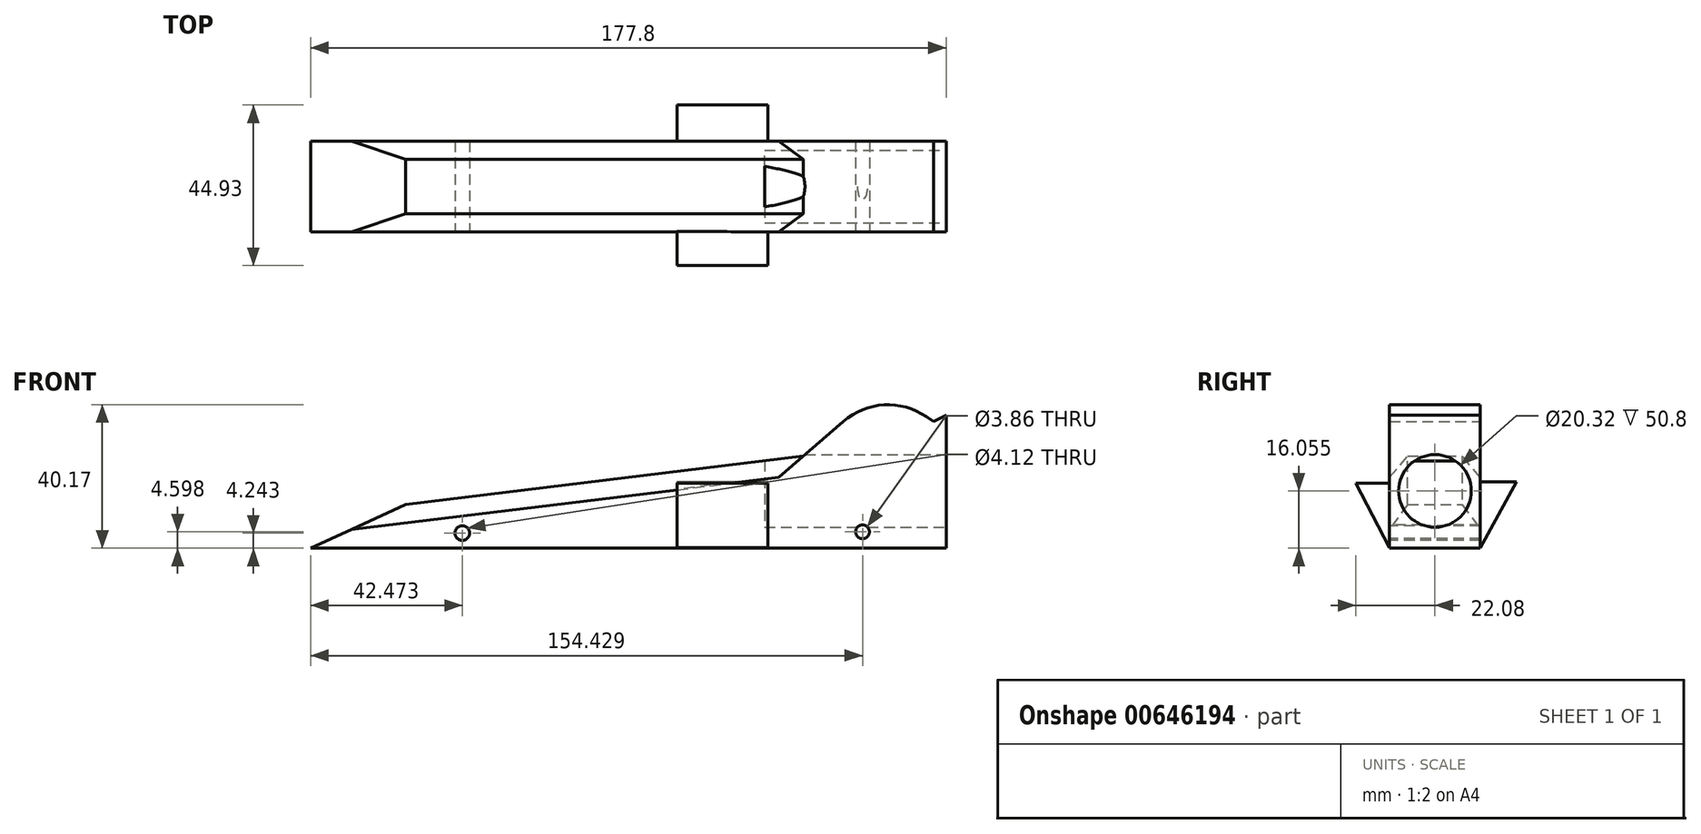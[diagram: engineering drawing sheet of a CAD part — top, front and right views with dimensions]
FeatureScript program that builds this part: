
annotation { "Feature Type Name" : "Feature", "Feature Type Description" : "" }
export const myFeature = defineFeature(function(context is Context, id is Id, definition is map)
    precondition{}
    {
        {
            var Q0;
            Q0=qCreatedBy(makeId("Front.planeOp"),FACE);
            var sketch = newSketch(context, id + "F0", { "sketchPlane" : qUnion([Q0])});
            skLineSegment(sketch, "E0", {"start": v(-102.57, 0) * mm, "end": v(75.23, 0) * mm});
            skLineSegment(sketch, "E1", {"start": v(75.23, 0) * mm, "end": v(75.23, 38.1) * mm});
            skLineSegment(sketch, "E2", {"start": v(-102.57, 0) * mm, "end": v(-75.96, 12.24) * mm});
            skLineSegment(sketch, "E3", {"start": v(-75.96, 12.24) * mm, "end": v(35.25, 25.78) * mm});
            skLineSegment(sketch, "E4", {"start": v(35.25, 25.78) * mm, "end": v(57.6, 45.15) * mm});
            skLineSegment(sketch, "E5", {"start": v(57.6, 45.15) * mm, "end": v(71.69, 35.47) * mm});
            skLineSegment(sketch, "E6", {"start": v(71.69, 35.47) * mm, "end": v(91.04, 45.49) * mm});
            skLineSegment(sketch, "E7", {"start": v(91.04, 45.49) * mm, "end": v(75.23, 38.1) * mm});
            skSolve(sketch);
        }
        {
            var Q0;
            Q0=makeQuery(id+"F0.imprint","IMPRINT",FACE,{"disambiguationData":[TD([[makeQuery(id+"F0.imprint","IMPRINT",EDGE,{"derivedFrom":sQuery(id+"F0.wireOp",EDGE,"E0")}),1.0]])]});
            extrude(context, id + "F1", {"entities" : qUnion([Q0]), "depth" : 25.4 * mm});
        }
        {
            var Q0;
            Q0=makeQuery(id+"F1.opExtrude","SWEPT_EDGE",EDGE,{"disambiguationData":[OSD([sQuery(id+"F0.wireOp",EDGE,"E4"),sQuery(id+"F0.wireOp",EDGE,"E5")])]});
            fillet(context, id + "F2", {"entities" : qUnion([Q0]), "radius" : 19 * mm, "tangentPropagation" : true, "allowEdgeOverflow" : false});
        }
        {
            var Q0;
            Q0=makeQuery(id+"F1.opExtrude","CAP_EDGE",EDGE,{"disambiguationData":[OSD([sQuery(id+"F0.wireOp",EDGE,"E3")])],"isStart":false});
            var Q1;
            Q1=makeQuery(id+"F1.opExtrude","CAP_EDGE",EDGE,{"disambiguationData":[OSD([sQuery(id+"F0.wireOp",EDGE,"E3")])],"isStart":true});
            chamfer(context, id + "F3", {"entities" : qUnion([Q0, Q1]), "width" : 5.08 * mm, "tangentPropagation" : true});
        }
        {
            var Q0;
            Q0=makeQuery(id+"F1.opExtrude","SWEPT_FACE",FACE,{"disambiguationData":[OSD([sQuery(id+"F0.wireOp",EDGE,"E1")])]});
            var sketch = newSketch(context, id + "F4", { "sketchPlane" : qUnion([Q0])});
            skCircle(sketch, "E8", {"center": v(-12.7, 16.05) * mm, "radius": 10.16 * mm});
            skSolve(sketch);
        }
        {
            var Q0;
            Q0=makeQuery(id+"F1.opExtrude","CAP_FACE",FACE,{"disambiguationData":[OSD([sQuery(id+"F0.wireOp",EDGE,"E0"),sQuery(id+"F0.wireOp",EDGE,"E1"),sQuery(id+"F0.wireOp",EDGE,"E2"),sQuery(id+"F0.wireOp",EDGE,"E3"),sQuery(id+"F0.wireOp",EDGE,"E4"),sQuery(id+"F0.wireOp",EDGE,"E5"),sQuery(id+"F0.wireOp",EDGE,"E6"),sQuery(id+"F0.wireOp",EDGE,"E7")])],"isStart":false});
            var sketch = newSketch(context, id + "F5", { "sketchPlane" : qUnion([Q0])});
            skCircle(sketch, "E9", {"center": v(-60.1, 4.24) * mm, "radius": 2.06 * mm});
            skCircle(sketch, "E10", {"center": v(51.86, 4.6) * mm, "radius": 1.93 * mm});
            skSolve(sketch);
        }
        {
            var Q0;
            Q0=qSketchRegion(id+"F5",true);
            extrude(context, id + "F6", {"entities" : qUnion([Q0]), "operationType" : NewBodyOperationType.REMOVE, "endBound" : BoundingType.THROUGH_ALL, "oppositeDirection" : true, "depth" : 25.4 * mm});
        }
        {
            var Q0;
            Q0=qSketchRegion(id+"F4",true);
            extrude(context, id + "F7", {"entities" : qUnion([Q0]), "operationType" : NewBodyOperationType.REMOVE, "oppositeDirection" : true, "depth" : 50.8 * mm});
        }
        {
            var Q0;
            Q0=qCreatedBy(makeId("Right.planeOp"),FACE);
            var sketch = newSketch(context, id + "F8", { "sketchPlane" : qUnion([Q0])});
            skLineSegment(sketch, "E11", {"start": v(0, 18.57) * mm, "end": v(10.15, 18.57) * mm});
            skLineSegment(sketch, "E12", {"start": v(10.15, 18.57) * mm, "end": v(0, 0) * mm});
            skLineSegment(sketch, "E13", {"start": v(0, 0) * mm, "end": v(0, 18.57) * mm});
            skLineSegment(sketch, "E14", {"start": v(-25.27, 18.2) * mm, "end": v(-34.78, 18.2) * mm});
            skLineSegment(sketch, "E15", {"start": v(-34.78, 18.2) * mm, "end": v(-25.32, 0) * mm});
            skLineSegment(sketch, "E16", {"start": v(-25.32, 0) * mm, "end": v(-25.27, 18.2) * mm});
            skSolve(sketch);
        }
        {
            var Q0;
            Q0=qSketchRegion(id+"F8",true);
            extrude(context, id + "F9", {"entities" : qUnion([Q0]), "operationType" : NewBodyOperationType.ADD, "depth" : 25.4 * mm});
        }
    });
